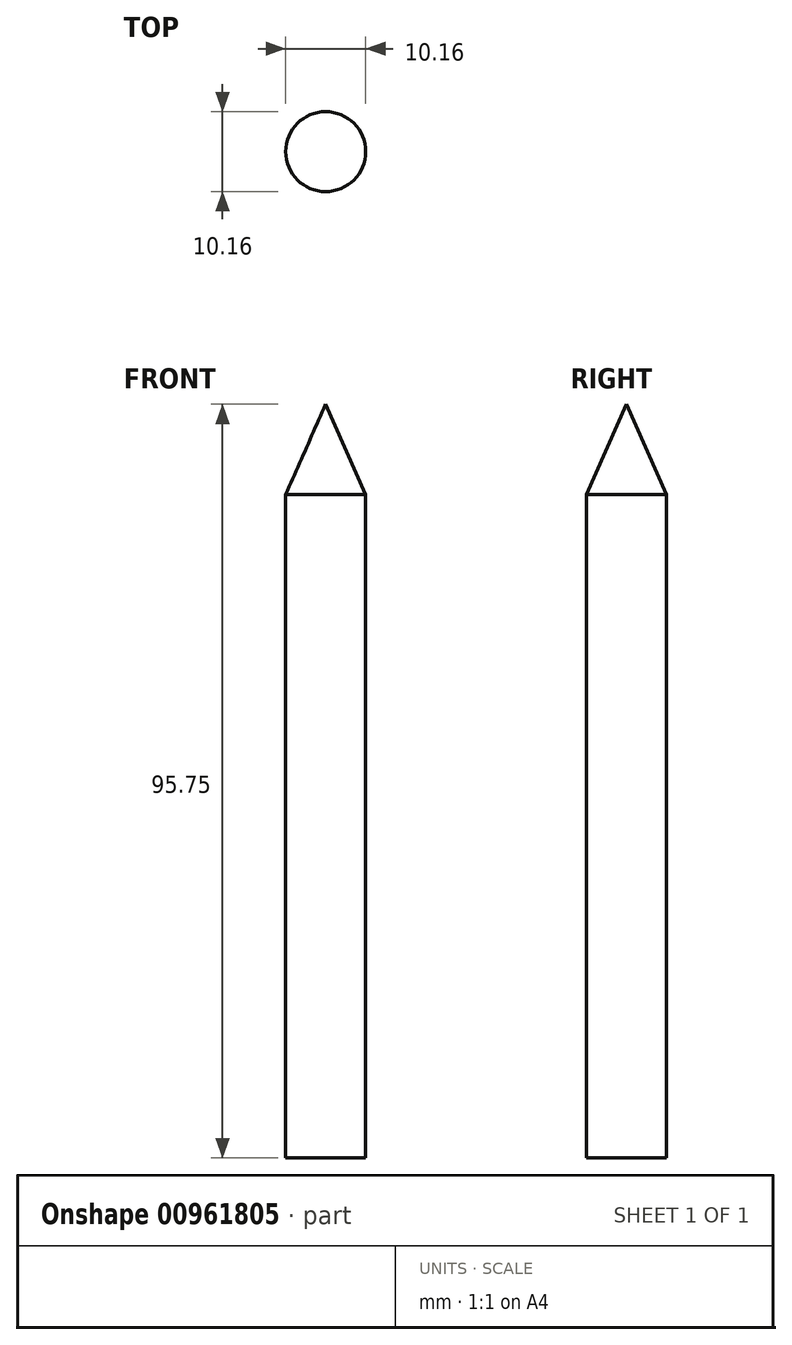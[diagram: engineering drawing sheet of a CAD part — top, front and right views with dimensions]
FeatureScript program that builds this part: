
annotation { "Feature Type Name" : "Feature", "Feature Type Description" : "" }
export const myFeature = defineFeature(function(context is Context, id is Id, definition is map)
    precondition{}
    {
        {
            var Q0;
            Q0=qCreatedBy(makeId("Front.planeOp"),FACE);
            var sketch = newSketch(context, id + "F0", { "sketchPlane" : qUnion([Q0])});
            skLineSegment(sketch, "E0", {"start": v(0, 38.53) * mm, "end": v(0, -57.22) * mm});
            skLineSegment(sketch, "E1", {"start": v(0, 38.53) * mm, "end": v(5.08, 27.05) * mm});
            skLineSegment(sketch, "E2", {"start": v(5.08, 27.05) * mm, "end": v(5.08, -57.22) * mm});
            skLineSegment(sketch, "E3", {"start": v(0, -57.22) * mm, "end": v(5.08, -57.22) * mm});
            skSolve(sketch);
        }
        {
            var Q0;
            Q0=makeQuery(id+"F0.imprint","IMPRINT",FACE,{"disambiguationData":[TD([[makeQuery(id+"F0.imprint","IMPRINT",EDGE,{"derivedFrom":sQuery(id+"F0.wireOp",EDGE,"E0")}),1.0]])]});
            var Q1;
            Q1=sQuery(id+"F0.wireOp",EDGE,"E0");
            revolve(context, id + "F1", {"surfaceOperationType" : NewSurfaceOperationType.NEW, "entities" : qUnion([Q0]), "axis" : qUnion([Q1]), "revolveType" : RevolveType.FULL});
        }
    });
